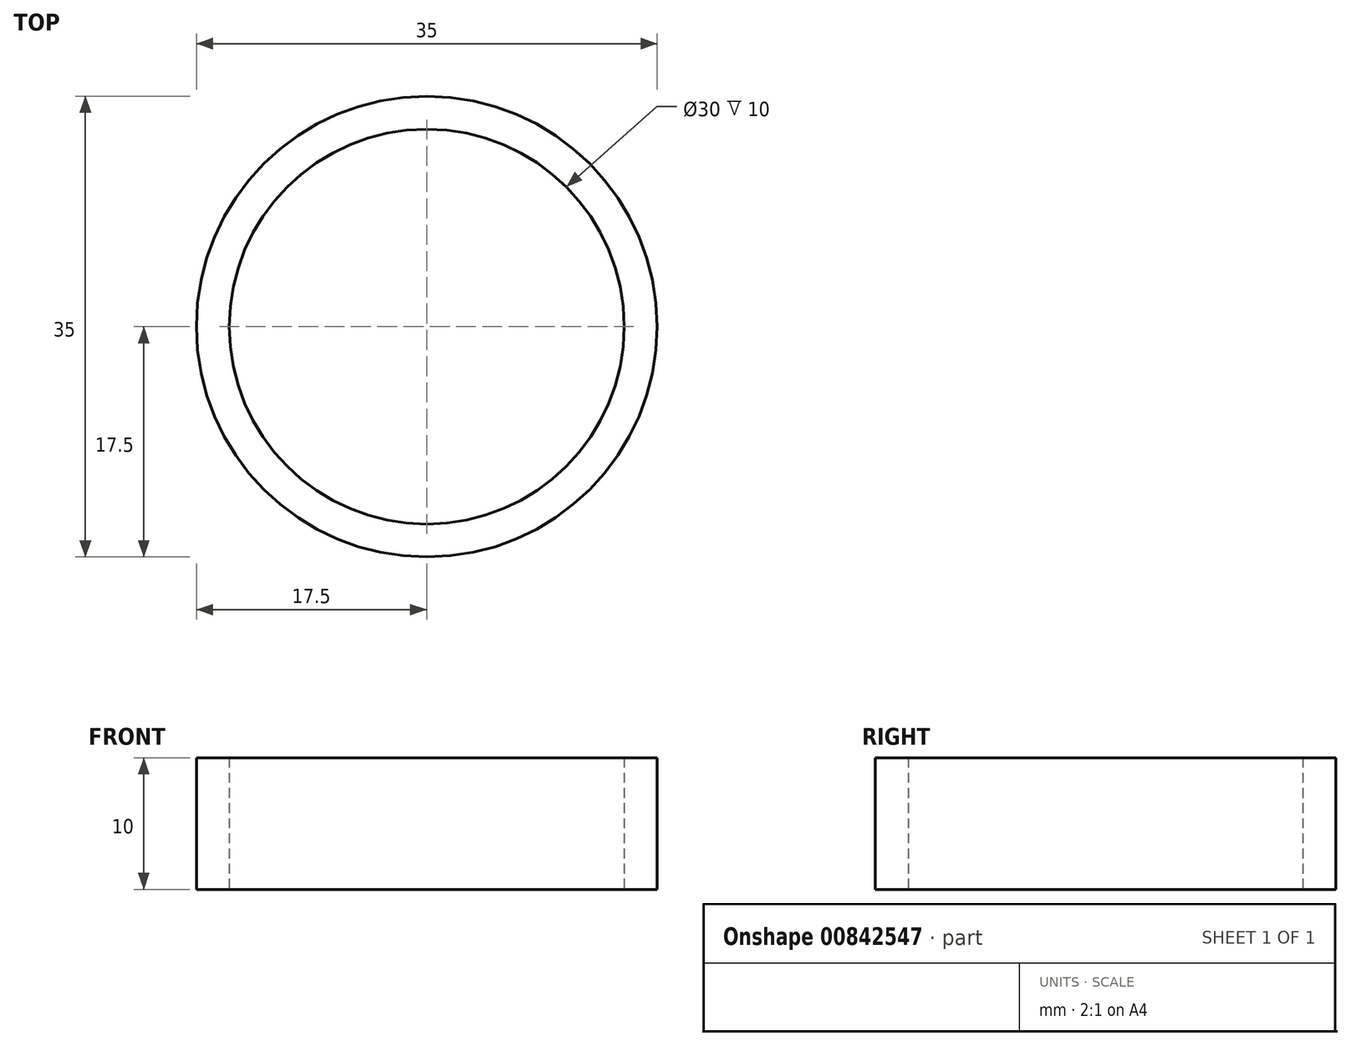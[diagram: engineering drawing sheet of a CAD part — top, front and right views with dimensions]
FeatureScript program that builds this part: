
annotation { "Feature Type Name" : "Feature", "Feature Type Description" : "" }
export const myFeature = defineFeature(function(context is Context, id is Id, definition is map)
    precondition{}
    {
        {
            var Q0;
            Q0=qCreatedBy(makeId("Top.planeOp"),FACE);
            var sketch = newSketch(context, id + "F0", { "sketchPlane" : qUnion([Q0])});
            skCircle(sketch, "E0", {"center": v(0, 0) * mm, "radius": 15 * mm});
            skCircle(sketch, "E1", {"center": v(0, 0) * mm, "radius": 17.5 * mm});
            skSolve(sketch);
        }
        {
            var Q0;
            Q0 = qSketchRegion(id + "F0", true);
            extrude(context, id + "F1", {"entities" : qUnion([Q0]), "depth" : 10 * mm, "offsetDistance" : 25 * mm});
        }
    });
